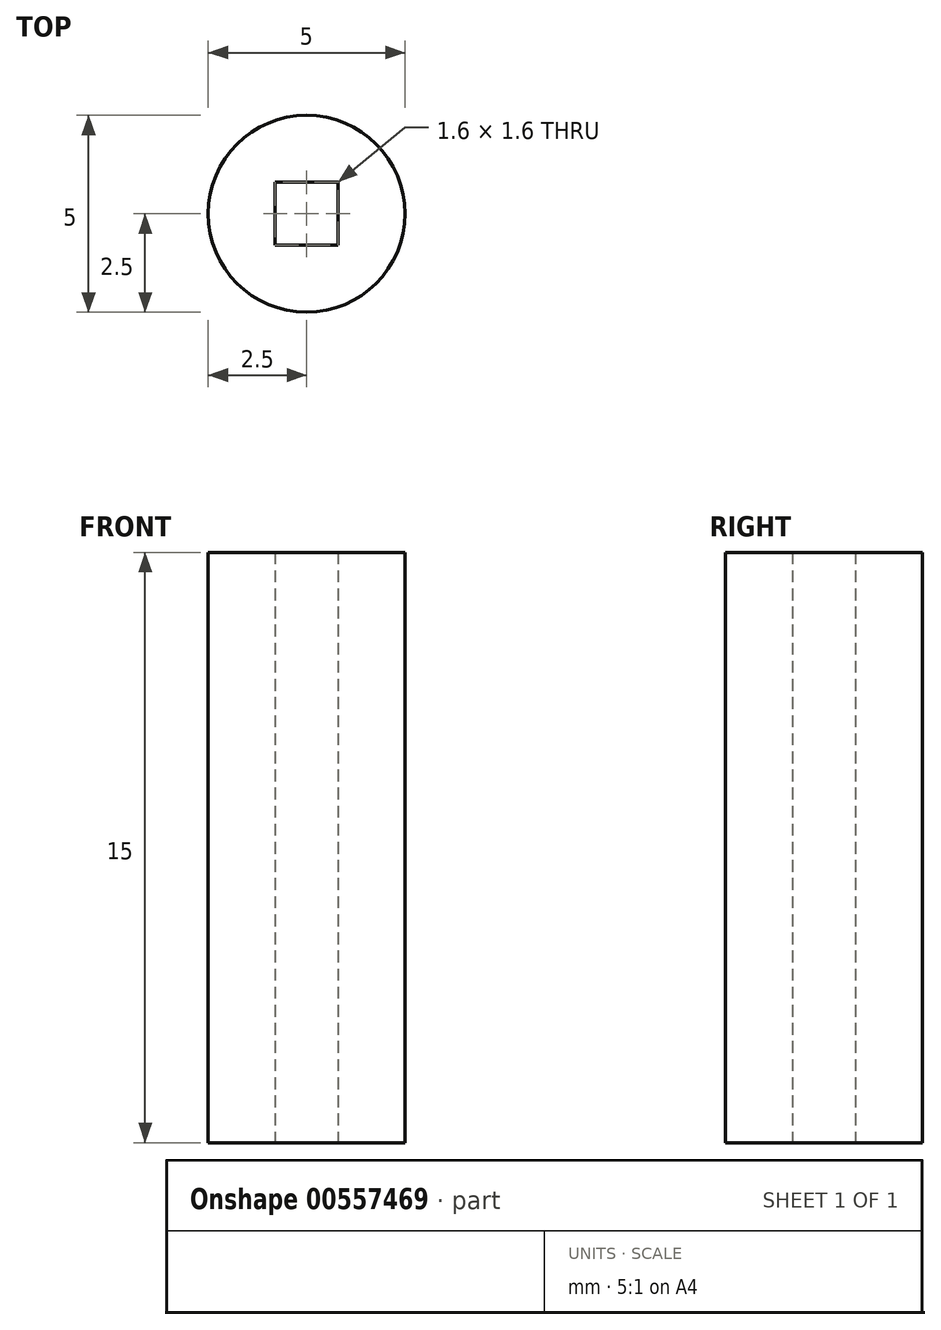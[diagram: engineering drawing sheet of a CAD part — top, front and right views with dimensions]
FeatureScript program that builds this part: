
annotation { "Feature Type Name" : "Feature", "Feature Type Description" : "" }
export const myFeature = defineFeature(function(context is Context, id is Id, definition is map)
    precondition{}
    {
        {
            var Q0;
            Q0=qCreatedBy(makeId("Top.planeOp"),FACE);
            var sketch = newSketch(context, id + "F0", { "sketchPlane" : qUnion([Q0])});
            skCircle(sketch, "E0", {"center": v(0, 0) * mm, "radius": 2.5 * mm});
            skLineSegment(sketch, "E1.bottom", {"start": v(-0.8, 0.8) * mm, "end": v(0.8, 0.8) * mm});
            skLineSegment(sketch, "E1.top", {"start": v(-0.8, -0.8) * mm, "end": v(0.8, -0.8) * mm});
            skLineSegment(sketch, "E1.left", {"start": v(-0.8, 0.8) * mm, "end": v(-0.8, -0.8) * mm});
            skLineSegment(sketch, "E1.right", {"start": v(0.8, 0.8) * mm, "end": v(0.8, -0.8) * mm});
            skSolve(sketch);
        }
        {
            var Q0;
            Q0=makeQuery(id+"F0.imprint","IMPRINT",FACE,{"disambiguationData":[TD([[makeQuery(id+"F0.imprint","IMPRINT",EDGE,{"derivedFrom":sQuery(id+"F0.wireOp",EDGE,"E0")}),1.0]])]});
            extrude(context, id + "F1", {"entities" : qUnion([Q0]), "depth" : 15 * mm, "offsetDistance" : 25 * mm});
        }
    });
